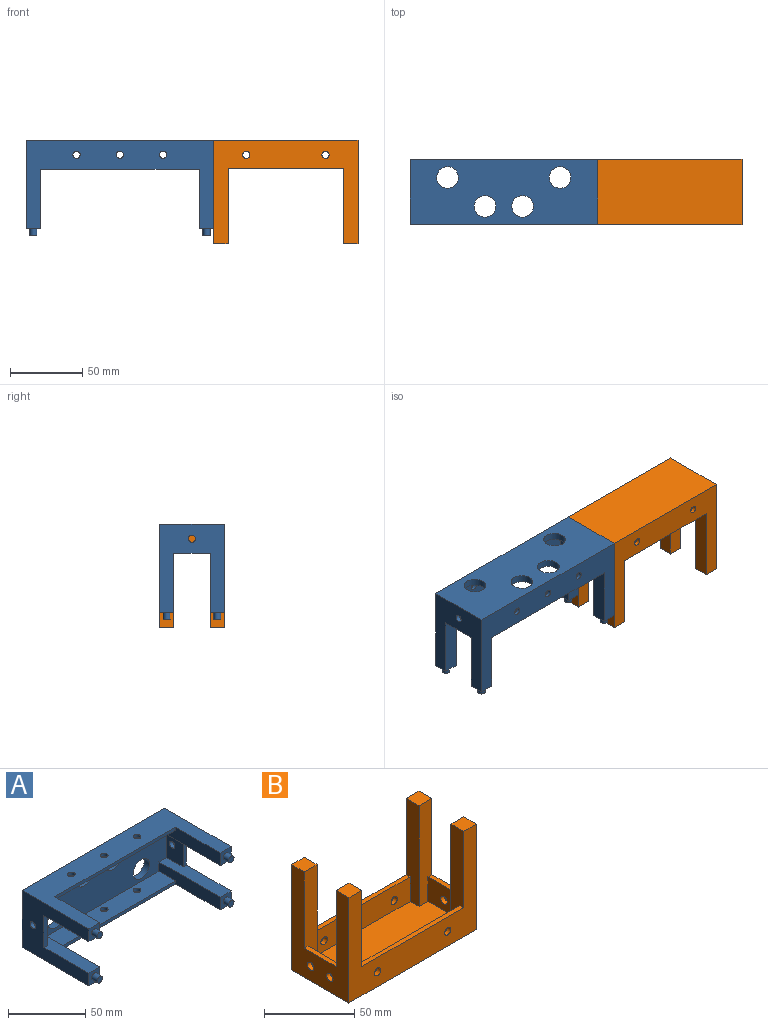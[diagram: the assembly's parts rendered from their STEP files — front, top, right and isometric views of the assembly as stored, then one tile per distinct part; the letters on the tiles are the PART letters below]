
ASSEMBLY  parts=2 mates=1
PART A: 46 faces, bbox 130x66x45 mm
  f0: plane 56x10mm, normal (0,0,1), area 515mm2, adj f1,f2,f4,f7,f22,f23
  f1: plane 124x40mm, normal (0,-1,0), area 4043.1mm2, adj f0,f2,f3,f15,f16,f17,f18,f19
  f2: plane 56x10mm, normal (1,0,0), area 522.5mm2, adj f0,f1,f6,f7,f11,f21
  f3: plane 56x10mm, normal (-1,0,0), area 522.5mm2, adj f1,f5,f12,f13,f17,f20
  f4: plane 61x45mm, normal (-1,0,0), area 1700.4mm2, adj f0,f7,f10,f11,f12,f14,f19,f23
  f5: plane 110x2.5mm, normal (0,-1,0), area 275mm2, adj f3,f12,f15,f20
  f6: plane 110x2.5mm, normal (0,-1,0), area 275mm2, adj f2,f11,f16,f21
  f7: plane 10x10mm, normal (0,-1,0), area 80.4mm2, adj f0,f2,f4,f11,f42
  f8: plane 10x10mm, normal (0,-1,0), area 80.4mm2, adj f9,f11,f16,f18,f44
  f9: plane 61x45mm, normal (1,0,0), area 1700.4mm2, adj f8,f11,f12,f13,f14,f17,f18,f25
  f10: plane 10x10mm, normal (0,-1,0), area 80.4mm2, adj f4,f12,f15,f19,f38
  f11: plane 130x61mm, normal (0,0,-1), area 3361.1mm2, adj f2,f4,f6,f7,f8,f9,f14,f16
  f12: plane 130x61mm, normal (0,0,1), area 3361.1mm2, adj f3,f4,f5,f9,f10,f13,f14,f15
  f13: plane 10x10mm, normal (0,-1,0), area 80.4mm2, adj f3,f9,f12,f17,f40
  f14: plane 130x45mm, normal (0,1,0), area 5143.1mm2, adj f4,f9,f11,f12,f26,f27,f28,f29
  f15: plane 56x10mm, normal (1,0,0), area 522.5mm2, adj f1,f5,f10,f12,f19,f20
  f16: plane 56x10mm, normal (-1,0,0), area 522.5mm2, adj f1,f6,f8,f11,f18,f21
  f17: plane 56x10mm, normal (0,0,-1), area 515mm2, adj f1,f3,f9,f13,f24,f25
  f18: plane 56x10mm, normal (0,0,1), area 515mm2, adj f1,f8,f9,f16,f24,f25
  f19: plane 56x10mm, normal (0,0,-1), area 515mm2, adj f1,f4,f10,f15,f22,f23
  f20: plane 110x15mm, normal (0,0,-1), area 1591.1mm2, adj f1,f3,f5,f15,f30,f31,f32
  f21: plane 110x15mm, normal (0,0,1), area 1591.1mm2, adj f1,f2,f6,f16,f34,f35,f36
  f22: plane 25x15mm, normal (1,0,0), area 355.4mm2, adj f0,f1,f19,f23,f37
  f23: plane 25x3mm, normal (0,-1,0), area 75mm2, adj f0,f4,f19,f22
  f24: plane 25x15mm, normal (-1,0,0), area 355.4mm2, adj f1,f17,f18,f25,f33
  f25: plane 25x3mm, normal (0,-1,0), area 75mm2, adj f9,f17,f18,f24
  f26: cylinder r=7.5mm len=15mm, axis (0,1,0), area 235.6mm2, adj f1,f14
  f27: cylinder r=7.5mm len=15mm, axis (0,1,0), area 235.6mm2, adj f1,f14
  f28: cylinder r=7.5mm len=15mm, axis (0,1,0), area 235.6mm2, adj f1,f14
  f29: cylinder r=7.5mm len=15mm, axis (0,1,0), area 235.6mm2, adj f1,f14
  f30: cylinder r=2.5mm len=5mm, axis (0,0,1), area 39.3mm2, adj f12,f20
  f31: cylinder r=2.5mm len=5mm, axis (0,0,1), area 39.3mm2, adj f12,f20
  f32: cylinder r=2.5mm len=5mm, axis (0,0,1), area 39.3mm2, adj f12,f20
  f33: cylinder r=2.5mm len=5mm, axis (1,0,0), area 47.1mm2, adj f9,f24
  f34: cylinder r=2.5mm len=5mm, axis (0,0,-1), area 39.3mm2, adj f11,f21
  f35: cylinder r=2.5mm len=5mm, axis (0,0,-1), area 39.3mm2, adj f11,f21
  f36: cylinder r=2.5mm len=5mm, axis (0,0,-1), area 39.3mm2, adj f11,f21
  f37: cylinder r=2.5mm len=5mm, axis (-1,0,0), area 47.1mm2, adj f4,f22
  f38: cylinder r=2.5mm len=5mm, axis (0,1,0), area 78.5mm2, adj f10,f39
  f39: plane 5x5mm, normal (0,-1,0), area 19.6mm2, adj f38
  f40: cylinder r=2.5mm len=5mm, axis (0,1,0), area 78.5mm2, adj f13,f41
  f41: plane 5x5mm, normal (0,-1,0), area 19.6mm2, adj f40
  f42: cylinder r=2.5mm len=5mm, axis (0,1,0), area 78.5mm2, adj f7,f43
  f43: plane 5x5mm, normal (0,-1,0), area 19.6mm2, adj f42
  f44: cylinder r=2.5mm len=5mm, axis (0,1,0), area 78.5mm2, adj f8,f45
  f45: plane 5x5mm, normal (0,-1,0), area 19.6mm2, adj f44
PART B: 33 faces, bbox 100x45x71.5 mm
  f0: plane 100x71.5mm, normal (0,1,0), area 2966.7mm2, adj f4,f7,f8,f10,f11,f19,f20,f25
  f1: plane 80x16.7mm, normal (0,-1,0), area 1296.7mm2, adj f19,f20,f21,f25,f31,f32
  f2: plane 100x71.5mm, normal (0,-1,0), area 2966.7mm2, adj f4,f6,f9,f10,f11,f14,f15,f23
  f3: plane 80x16.7mm, normal (0,1,0), area 1296.7mm2, adj f14,f15,f21,f23,f29,f30
  f4: plane 71.5x45mm, normal (-1,0,0), area 1883.2mm2, adj f0,f2,f7,f9,f11,f12,f13,f24
  f5: plane 25x16.7mm, normal (1,0,0), area 378.2mm2, adj f12,f13,f21,f24,f27,f28
  f6: plane 10x10mm, normal (0,0,1), area 100mm2, adj f2,f10,f15,f16
  f7: plane 10x10mm, normal (0,0,1), area 100mm2, adj f0,f4,f12,f20
  f8: plane 10x10mm, normal (0,0,1), area 100mm2, adj f0,f10,f18,f19
  f9: plane 10x10mm, normal (0,0,1), area 100mm2, adj f2,f4,f13,f14
  f10: plane 71.5x45mm, normal (1,0,0), area 1902.9mm2, adj f0,f2,f6,f8,f11,f16,f18,f22
  f11: plane 100x45mm, normal (0,0,-1), area 4500mm2, adj f0,f2,f4,f10
  f12: plane 68.5x10mm, normal (0,-1,0), area 634.9mm2, adj f4,f5,f7,f20,f21,f24
  f13: plane 68.5x10mm, normal (0,1,0), area 634.9mm2, adj f4,f5,f9,f14,f21,f24
  f14: plane 68.5x10mm, normal (1,0,0), area 634.9mm2, adj f2,f3,f9,f13,f21,f23
  f15: plane 68.5x10mm, normal (-1,0,0), area 634.9mm2, adj f2,f3,f6,f16,f21,f23
  f16: plane 68.5x10mm, normal (0,1,0), area 634.9mm2, adj f6,f10,f15,f17,f21,f22
  f17: plane 25x16.7mm, normal (-1,0,0), area 397.9mm2, adj f16,f18,f21,f22,f26
  f18: plane 68.5x10mm, normal (0,-1,0), area 634.9mm2, adj f8,f10,f17,f19,f21,f22
  f19: plane 68.5x10mm, normal (-1,0,0), area 634.9mm2, adj f0,f1,f8,f18,f21,f25
  f20: plane 68.5x10mm, normal (1,0,0), area 634.9mm2, adj f0,f1,f7,f12,f21,f25
  f21: plane 94x39mm, normal (0,0,1), area 3470mm2, adj f1,f3,f5,f12,f13,f14,f15,f16
  f22: plane 25x3mm, normal (0,0,1), area 75mm2, adj f10,f16,f17,f18
  f23: plane 80x3mm, normal (0,0,1), area 240mm2, adj f2,f3,f14,f15
  f24: plane 25x3mm, normal (0,0,1), area 75mm2, adj f4,f5,f12,f13
  f25: plane 80x3mm, normal (0,0,1), area 240mm2, adj f0,f1,f19,f20
  f26: cylinder r=2.5mm len=5mm, axis (1,0,0), area 47.1mm2, adj f10,f17
  f27: cylinder r=2.5mm len=5mm, axis (-1,0,0), area 47.1mm2, adj f4,f5
  f28: cylinder r=2.5mm len=5mm, axis (-1,0,0), area 47.1mm2, adj f4,f5
  f29: cylinder r=2.5mm len=5mm, axis (0,-1,0), area 47.1mm2, adj f2,f3
  f30: cylinder r=2.5mm len=5mm, axis (0,-1,0), area 47.1mm2, adj f2,f3
  f31: cylinder r=2.5mm len=5mm, axis (0,1,0), area 47.1mm2, adj f0,f1
  f32: cylinder r=2.5mm len=5mm, axis (0,1,0), area 47.1mm2, adj f0,f1
PLACE A rot(axis=(1,0,0),90deg) t=(-62.06,-61.01,-35.35)mm
PLACE B rot(axis=(0,1,0),180deg) t=(52.94,-61.01,-35.35)mm
MATE fastened B.f26 <-> A.f33  axis (-1,0,0) through (2.94,-61.01,-45.35)mm
